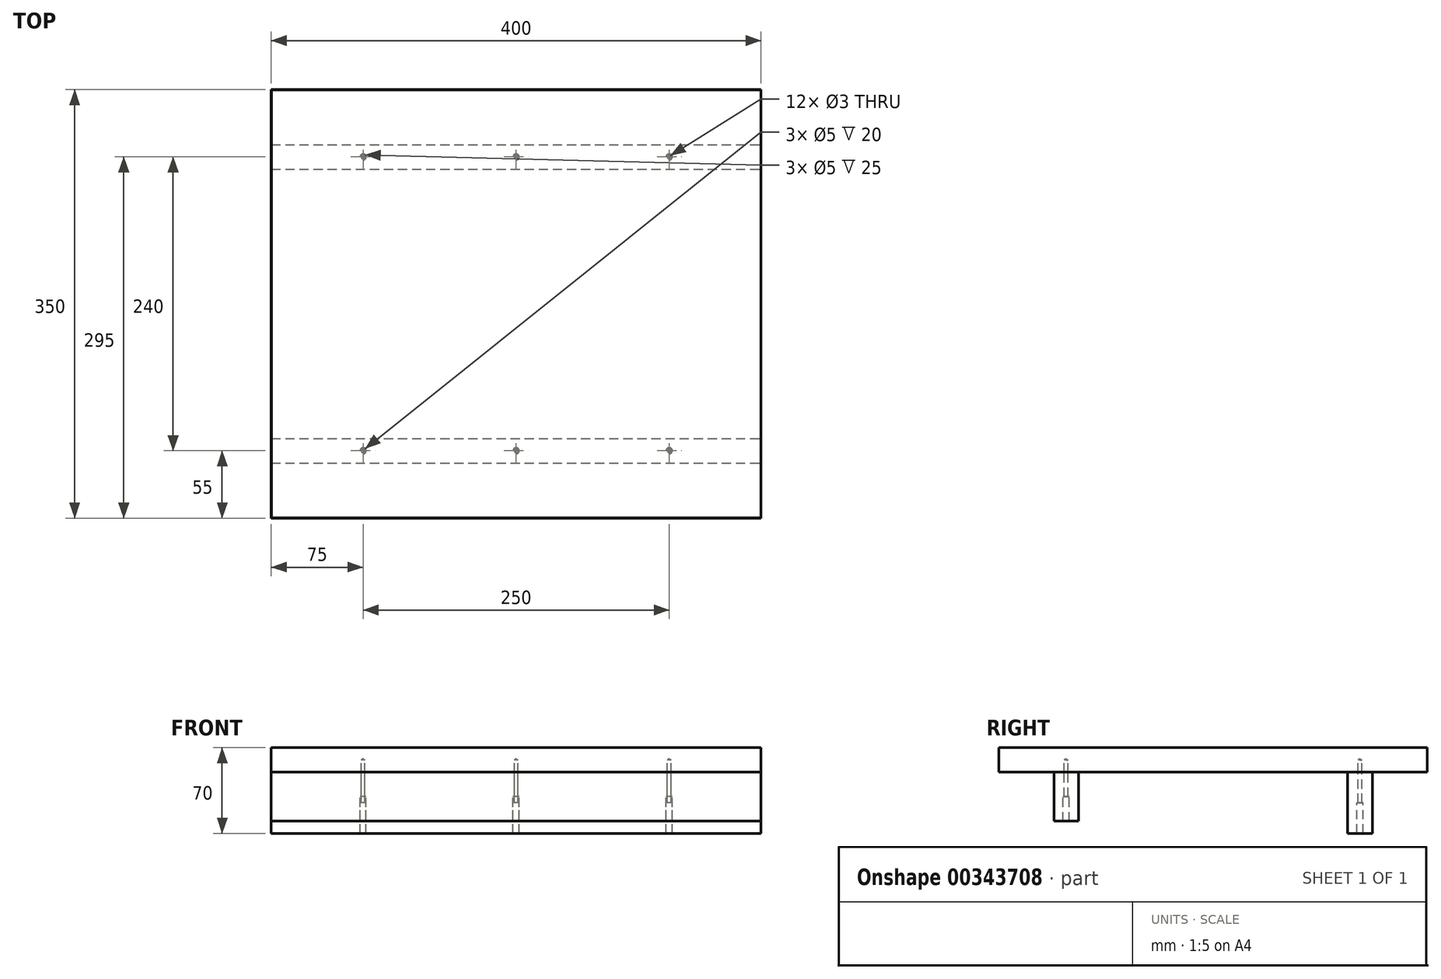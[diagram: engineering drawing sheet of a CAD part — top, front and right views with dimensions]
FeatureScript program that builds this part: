
annotation { "Feature Type Name" : "Feature", "Feature Type Description" : "" }
export const myFeature = defineFeature(function(context is Context, id is Id, definition is map)
    precondition{}
    {
        {
            var Q0;
            Q0=qCreatedBy(makeId("Top.planeOp"),FACE);
            var sketch = newSketch(context, id + "F0", { "sketchPlane" : qUnion([Q0])});
            skLineSegment(sketch, "E0.bottom", {"start": v(200, 175) * mm, "end": v(-200, 175) * mm});
            skLineSegment(sketch, "E0.top", {"start": v(200, -175) * mm, "end": v(-200, -175) * mm});
            skLineSegment(sketch, "E0.left", {"start": v(200, 175) * mm, "end": v(200, -175) * mm});
            skLineSegment(sketch, "E0.right", {"start": v(-200, 175) * mm, "end": v(-200, -175) * mm});
            skPoint(sketch, "E0.middle", {"position": v(0, 0) * mm});
            skLineSegment(sketch, "E1.bottom", {"start": v(-200, 110) * mm, "end": v(200, 110) * mm});
            skLineSegment(sketch, "E1.top", {"start": v(-200, 130) * mm, "end": v(200, 130) * mm});
            skLineSegment(sketch, "E1.left", {"start": v(-200, 130) * mm, "end": v(-200, 110) * mm});
            skLineSegment(sketch, "E1.right", {"start": v(200, 130) * mm, "end": v(200, 110) * mm});
            skLineSegment(sketch, "E2.bottom", {"start": v(-200, -110) * mm, "end": v(200, -110) * mm});
            skLineSegment(sketch, "E2.top", {"start": v(-200, -130) * mm, "end": v(200, -130) * mm});
            skLineSegment(sketch, "E2.left", {"start": v(-200, -110) * mm, "end": v(-200, -130) * mm});
            skLineSegment(sketch, "E2.right", {"start": v(200, -110) * mm, "end": v(200, -130) * mm});
            skSolve(sketch);
        }
        {
            var Q0;
            Q0 = qSketchRegion(id + "F0", true);
            extrude(context, id + "F1", {"entities" : qUnion([Q0]), "depth" : 20 * mm});
        }
        {
            var Q0;
            Q0=makeQuery(id+"F0.imprint","IMPRINT",FACE,{"disambiguationData":[TD([[makeQuery(id+"F0.imprint","IMPRINT",EDGE,{"derivedFrom":sQuery(id+"F0.wireOp",EDGE,"E2.bottom")}),-1.0]])]});
            var Q1;
            Q1=sQuery(id+"F0.wireOp",EDGE,"E2.bottom");
            var Q2;
            Q2=sQuery(id+"F0.wireOp",EDGE,"E2.top");
            var Q3;
            Q3=sQuery(id+"F0.wireOp",EDGE,"E2.right");
            var Q4;
            Q4=sQuery(id+"F0.wireOp",EDGE,"E2.left");
            extrude(context, id + "F2", {"entities" : qUnion([Q0]), "surfaceEntities" : qUnion([Q1, Q2, Q3, Q4]), "oppositeDirection" : true, "depth" : 40 * mm});
        }
        {
            var Q0;
            Q0=makeQuery(id+"F0.imprint","IMPRINT",FACE,{"disambiguationData":[TD([[makeQuery(id+"F0.imprint","IMPRINT",EDGE,{"derivedFrom":sQuery(id+"F0.wireOp",EDGE,"E1.bottom")}),1.0]])]});
            extrude(context, id + "F3", {"entities" : qUnion([Q0]), "oppositeDirection" : true, "depth" : 50 * mm});
        }
        {
            var Q0;
            Q0=makeQuery(id+"F2.opExtrude","CAP_VERTEX",VERTEX,{"disambiguationData":[OSD([sQuery(id+"F0.wireOp",EDGE,"E0.left"),sQuery(id+"F0.wireOp",EDGE,"E2.top"),sQuery(id+"F0.wireOp",EDGE,"E2.right")])],"isStart":false});
            var Q1;
            Q1=makeQuery(id+"F2.opExtrude","CAP_VERTEX",VERTEX,{"disambiguationData":[OSD([sQuery(id+"F0.wireOp",EDGE,"E0.left"),sQuery(id+"F0.wireOp",EDGE,"E2.bottom"),sQuery(id+"F0.wireOp",EDGE,"E2.right")])],"isStart":false});
            var Q2;
            Q2=makeQuery(id+"F2.opExtrude","CAP_VERTEX",VERTEX,{"disambiguationData":[OSD([sQuery(id+"F0.wireOp",EDGE,"E0.right"),sQuery(id+"F0.wireOp",EDGE,"E2.bottom"),sQuery(id+"F0.wireOp",EDGE,"E2.left")])],"isStart":false});
            cPlane(context, id + "F4", {"entities" : qUnion([Q0, Q1, Q2]), "cplaneType" : CPlaneType.THREE_POINT, "offset" : 25 * mm, "width" : 150 * mm, "height" : 150 * mm});
        }
        {
            var Q0;
            Q0=qCreatedBy(id+"F4.planeOp",FACE);
            var sketch = newSketch(context, id + "F5", { "sketchPlane" : qUnion([Q0])});
            skPoint(sketch, "E3", {"position": v(-125, 120) * mm});
            skPoint(sketch, "E4", {"position": v(0, 120) * mm});
            skPoint(sketch, "E5", {"position": v(125, 120) * mm});
            skSolve(sketch);
        }
        {
            var Q0;
            Q0=sQuery(id+"F5.wireOp",VERTEX,"E3");
            var Q1;
            Q1=sQuery(id+"F5.wireOp",VERTEX,"E4");
            var Q2;
            Q2=sQuery(id+"F5.wireOp",VERTEX,"E5");
            var Q3;
            Q3=makeQuery(id+"F2.opExtrude","SWEPT_BODY",BODY,{"disambiguationData":[OSD([sQuery(id+"F0.wireOp",EDGE,"E2.bottom"),sQuery(id+"F0.wireOp",EDGE,"E2.top"),sQuery(id+"F0.wireOp",EDGE,"E2.left"),sQuery(id+"F0.wireOp",EDGE,"E2.right")])]});
            var Q4;
            Q4=makeQuery(id+"F1.opExtrude","SWEPT_BODY",BODY,{"disambiguationData":[OSD([sQuery(id+"F0.wireOp",EDGE,"E0.bottom"),sQuery(id+"F0.wireOp",EDGE,"E0.top"),sQuery(id+"F0.wireOp",EDGE,"E0.left"),sQuery(id+"F0.wireOp",EDGE,"E0.right"),sQuery(id+"F0.wireOp",EDGE,"E1.left"),sQuery(id+"F0.wireOp",EDGE,"E1.right"),sQuery(id+"F0.wireOp",EDGE,"E2.left"),sQuery(id+"F0.wireOp",EDGE,"E2.right")])]});
            hole(context, id + "F6", {"style" : HoleStyle.C_BORE, "endStyle" : HoleEndStyle.BLIND, "holeDiameter" : 3 * mm, "cBoreDiameter" : 5 * mm, "cBoreDepth" : 20 * mm, "holeDepth" : 50 * mm, "isTappedThrough" : true, "tappedDepth" : 12 * mm, "tapClearance" : 3, "locations" : qUnion([Q0, Q1, Q2]), "scope" : qUnion([Q3, Q4]), "startStyle" : HoleStartStyle.PART});
        }
        {
            var Q0;
            Q0=makeQuery(id+"F3.opExtrude","CAP_VERTEX",VERTEX,{"disambiguationData":[OSD([sQuery(id+"F0.wireOp",EDGE,"E0.right"),sQuery(id+"F0.wireOp",EDGE,"E1.top"),sQuery(id+"F0.wireOp",EDGE,"E1.left")])],"isStart":false});
            var Q1;
            Q1=makeQuery(id+"F3.opExtrude","CAP_VERTEX",VERTEX,{"disambiguationData":[OSD([sQuery(id+"F0.wireOp",EDGE,"E0.right"),sQuery(id+"F0.wireOp",EDGE,"E1.bottom"),sQuery(id+"F0.wireOp",EDGE,"E1.left")])],"isStart":false});
            var Q2;
            Q2=makeQuery(id+"F3.opExtrude","CAP_VERTEX",VERTEX,{"disambiguationData":[OSD([sQuery(id+"F0.wireOp",EDGE,"E0.left"),sQuery(id+"F0.wireOp",EDGE,"E1.bottom"),sQuery(id+"F0.wireOp",EDGE,"E1.right")])],"isStart":false});
            cPlane(context, id + "F7", {"entities" : qUnion([Q0, Q1, Q2]), "cplaneType" : CPlaneType.THREE_POINT, "offset" : 25 * mm, "width" : 150 * mm, "height" : 150 * mm});
        }
        {
            var Q0;
            Q0=qCreatedBy(id+"F7.planeOp",FACE);
            var sketch = newSketch(context, id + "F8", { "sketchPlane" : qUnion([Q0])});
            skPoint(sketch, "E6", {"position": v(-125, -120) * mm});
            skPoint(sketch, "E7", {"position": v(0, -120) * mm});
            skPoint(sketch, "E8", {"position": v(125, -120) * mm});
            skSolve(sketch);
        }
        {
            var Q0;
            Q0=sQuery(id+"F8.wireOp",VERTEX,"E8");
            var Q1;
            Q1=sQuery(id+"F8.wireOp",VERTEX,"E7");
            var Q2;
            Q2=sQuery(id+"F8.wireOp",VERTEX,"E6");
            var Q3;
            Q3=makeQuery(id+"F3.opExtrude","SWEPT_BODY",BODY,{"disambiguationData":[OSD([sQuery(id+"F0.wireOp",EDGE,"E1.bottom"),sQuery(id+"F0.wireOp",EDGE,"E1.top"),sQuery(id+"F0.wireOp",EDGE,"E1.left"),sQuery(id+"F0.wireOp",EDGE,"E1.right")])]});
            var Q4;
            Q4=makeQuery(id+"F1.opExtrude","SWEPT_BODY",BODY,{"disambiguationData":[OSD([sQuery(id+"F0.wireOp",EDGE,"E0.bottom"),sQuery(id+"F0.wireOp",EDGE,"E0.top"),sQuery(id+"F0.wireOp",EDGE,"E0.left"),sQuery(id+"F0.wireOp",EDGE,"E0.right"),sQuery(id+"F0.wireOp",EDGE,"E1.left"),sQuery(id+"F0.wireOp",EDGE,"E1.right"),sQuery(id+"F0.wireOp",EDGE,"E2.left"),sQuery(id+"F0.wireOp",EDGE,"E2.right")])]});
            hole(context, id + "F9", {"style" : HoleStyle.C_BORE, "endStyle" : HoleEndStyle.BLIND, "holeDiameter" : 3 * mm, "cBoreDiameter" : 5 * mm, "cBoreDepth" : 25 * mm, "holeDepth" : 60 * mm, "isTappedThrough" : true, "tappedDepth" : 12 * mm, "tapClearance" : 3, "locations" : qUnion([Q0, Q1, Q2]), "scope" : qUnion([Q3, Q4]), "startStyle" : HoleStartStyle.PART});
        }
        {
            var Q0;
            Q0=makeQuery(id+"F1.opExtrude","CAP_EDGE",EDGE,{"disambiguationData":[OSD([sQuery(id+"F0.wireOp",EDGE,"E0.right"),sQuery(id+"F0.wireOp",EDGE,"E1.left"),sQuery(id+"F0.wireOp",EDGE,"E2.left")])],"isStart":false});
            var Q1;
            Q1=makeQuery(id+"F1.opExtrude","CAP_EDGE",EDGE,{"disambiguationData":[OSD([sQuery(id+"F0.wireOp",EDGE,"E0.top")])],"isStart":false});
            var Q2;
            Q2=makeQuery(id+"F1.opExtrude","CAP_EDGE",EDGE,{"disambiguationData":[OSD([sQuery(id+"F0.wireOp",EDGE,"E0.left"),sQuery(id+"F0.wireOp",EDGE,"E1.right"),sQuery(id+"F0.wireOp",EDGE,"E2.right")])],"isStart":false});
            var Q3;
            Q3=makeQuery(id+"F1.opExtrude","CAP_EDGE",EDGE,{"disambiguationData":[OSD([sQuery(id+"F0.wireOp",EDGE,"E0.bottom")])],"isStart":false});
            chamfer(context, id + "F10", {"entities" : qUnion([Q0, Q1, Q2, Q3]), "width" : 0.1 * mm, "tangentPropagation" : true});
        }
    });
